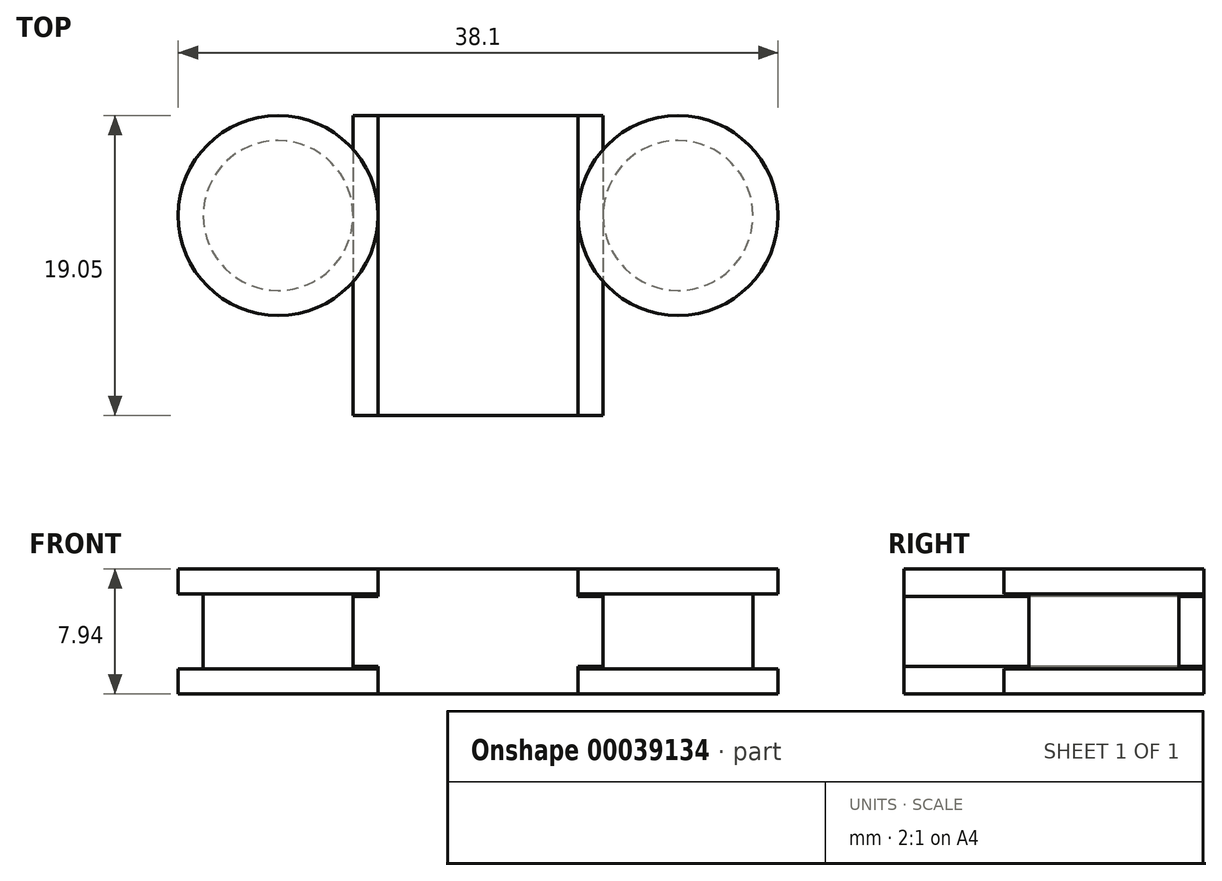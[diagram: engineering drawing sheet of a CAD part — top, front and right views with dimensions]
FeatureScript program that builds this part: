
annotation { "Feature Type Name" : "Feature", "Feature Type Description" : "" }
export const myFeature = defineFeature(function(context is Context, id is Id, definition is map)
    precondition{}
    {
        {
            var Q0;
            Q0=qCreatedBy(makeId("Top.planeOp"),FACE);
            var sketch = newSketch(context, id + "F0", { "sketchPlane" : qUnion([Q0])});
            skCircle(sketch, "E0", {"center": v(25.4, 0) * mm, "radius": 6.35 * mm});
            skCircle(sketch, "E1", {"center": v(0, 0) * mm, "radius": 6.35 * mm});
            skSolve(sketch);
        }
        {
            var Q0;
            Q0 = qSketchRegion(id + "F0", true);
            extrude(context, id + "F1", {"entities" : qUnion([Q0]), "depth" : 1.59 * mm});
        }
        {
            var Q0;
            Q0=makeQuery(id+"F1.opExtrude","CAP_FACE",FACE,{"disambiguationData":[OSD([sQuery(id+"F0.wireOp",EDGE,"E1")])],"isStart":false});
            var sketch = newSketch(context, id + "F2", { "sketchPlane" : qUnion([Q0])});
            skCircle(sketch, "E2", {"center": v(0, 0) * mm, "radius": 4.76 * mm});
            skCircle(sketch, "E3", {"center": v(25.4, 0) * mm, "radius": 4.76 * mm});
            skSolve(sketch);
        }
        {
            var Q0;
            Q0 = qSketchRegion(id + "F2", true);
            extrude(context, id + "F3", {"entities" : qUnion([Q0]), "operationType" : NewBodyOperationType.ADD, "depth" : 6.35 * mm});
        }
        {
            var Q0;
            Q0=makeQuery(id+"F3.opExtrude","CAP_FACE",FACE,{"disambiguationData":[OSD([sQuery(id+"F2.wireOp",EDGE,"E2")])],"isStart":false});
            var sketch = newSketch(context, id + "F4", { "sketchPlane" : qUnion([Q0])});
            skCircle(sketch, "E4.0.0", {"center": v(25.4, 0) * mm, "radius": 6.35 * mm});
            skCircle(sketch, "E4.2.0", {"center": v(0, 0) * mm, "radius": 6.35 * mm});
            skSolve(sketch);
        }
        {
            var Q0;
            {var subQ0=sQuery(id+"F4.wireOp",EDGE,"E4.1.0");var subQ2=makeQuery(id+"F4.imprint","INTERSECT",VERTEX,{"derivedFrom":[sQuery(id+"F4.wireOp",EDGE,"E4.0.0"),subQ0]});Q0=makeQuery(id+"F4.imprint","IMPRINT",FACE,{"disambiguationData":[TD([[makeQuery(id+"F4.imprint","IMPRINT",EDGE,{"disambiguationData":[TD([[subQ2,-1.0]])],"derivedFrom":subQ0}),1.0]])]});}
            var Q1;
            Q1=makeQuery(id+"F4.imprint","IMPRINT",FACE,{"disambiguationData":[TD([[makeQuery(id+"F4.imprint","IMPRINT",EDGE,{"derivedFrom":sQuery(id+"F4.wireOp",EDGE,"E4.2.0")}),1.0]])]});
            var Q2;
            Q2=makeQuery(id+"F4.imprint","IMPRINT",FACE,{"disambiguationData":[TD([[makeQuery(id+"F4.imprint","IMPRINT",EDGE,{"derivedFrom":sQuery(id+"F4.wireOp",EDGE,"E4.0.0")}),1.0]])]});
            extrude(context, id + "F5", {"entities" : qUnion([Q0, Q1, Q2]), "operationType" : NewBodyOperationType.ADD, "oppositeDirection" : true, "depth" : 1.59 * mm});
        }
        {
            var Q0;
            {var subQ0=sQuery(id+"F2.wireOp",EDGE,"E2");Q0=makeQuery(id+"F5.boolean.opBoolean","MERGE",FACE,{"derivedFrom":[makeQuery(id+"F3.opExtrude","CAP_FACE",FACE,{"disambiguationData":[OSD([subQ0])],"isStart":false}),makeQuery(id+"F5.opExtrude","CAP_FACE",FACE,{"disambiguationData":[OSD([subQ0,sQuery(id+"F4.wireOp",EDGE,"E4.2.0")])],"isStart":true})]});}
            var sketch = newSketch(context, id + "F6", { "sketchPlane" : qUnion([Q0])});
            skLineSegment(sketch, "E5.rect.bottom", {"start": v(19.05, 6.35) * mm, "end": v(6.35, 6.35) * mm});
            skLineSegment(sketch, "E5.rect.top", {"start": v(19.05, -12.7) * mm, "end": v(6.35, -12.7) * mm});
            skLineSegment(sketch, "E5.rect.left", {"start": v(19.05, 6.35) * mm, "end": v(19.05, -12.7) * mm});
            skLineSegment(sketch, "E5.rect.right", {"start": v(6.35, 6.35) * mm, "end": v(6.35, -12.7) * mm});
            skPoint(sketch, "E5.rect.middle", {"position": v(12.7, -3.17) * mm});
            skSolve(sketch);
        }
        {
            var Q0;
            Q0 = qSketchRegion(id + "F6", true);
            var Q1;
            Q1=makeQuery(id+"F1.opExtrude","CAP_FACE",FACE,{"disambiguationData":[OSD([sQuery(id+"F0.wireOp",EDGE,"E1")])],"isStart":true});
            extrude(context, id + "F7", {"entities" : qUnion([Q0]), "endBound" : BoundingType.UP_TO_SURFACE, "oppositeDirection" : true, "endBoundEntityFace" : qUnion([Q1]), "depth" : 25.4 * mm});
        }
        {
            var Q0;
            Q0=makeQuery(id+"F7.opExtrude","SWEPT_FACE",FACE,{"disambiguationData":[OSD([sQuery(id+"F6.wireOp",EDGE,"E5.rect.top")])]});
            var sketch = newSketch(context, id + "F8", { "sketchPlane" : qUnion([Q0])});
            skLineSegment(sketch, "E6.bottom", {"start": v(4.76, 6.2) * mm, "end": v(20.64, 6.2) * mm});
            skLineSegment(sketch, "E6.top", {"start": v(4.76, 1.75) * mm, "end": v(20.64, 1.75) * mm});
            skLineSegment(sketch, "E6.left", {"start": v(4.76, 6.2) * mm, "end": v(4.76, 1.75) * mm});
            skLineSegment(sketch, "E6.right", {"start": v(20.64, 6.2) * mm, "end": v(20.64, 1.75) * mm});
            skLineSegment(sketch, "E7", {"start": v(12.7, 7.94) * mm, "end": v(12.7, -2.46) * mm, "construction": true});
            skLineSegment(sketch, "E8", {"start": v(19.05, 3.97) * mm, "end": v(-6.26, 3.97) * mm, "construction": true});
            skSolve(sketch);
        }
        {
            var Q0;
            Q0 = qSketchRegion(id + "F8", true);
            var Q1;
            Q1=makeQuery(id+"F7.opExtrude","SWEPT_FACE",FACE,{"disambiguationData":[OSD([sQuery(id+"F6.wireOp",EDGE,"E5.rect.bottom")])]});
            extrude(context, id + "F9", {"entities" : qUnion([Q0]), "operationType" : NewBodyOperationType.ADD, "endBound" : BoundingType.UP_TO_SURFACE, "oppositeDirection" : true, "endBoundEntityFace" : qUnion([Q1]), "depth" : 25.4 * mm});
        }
    });
